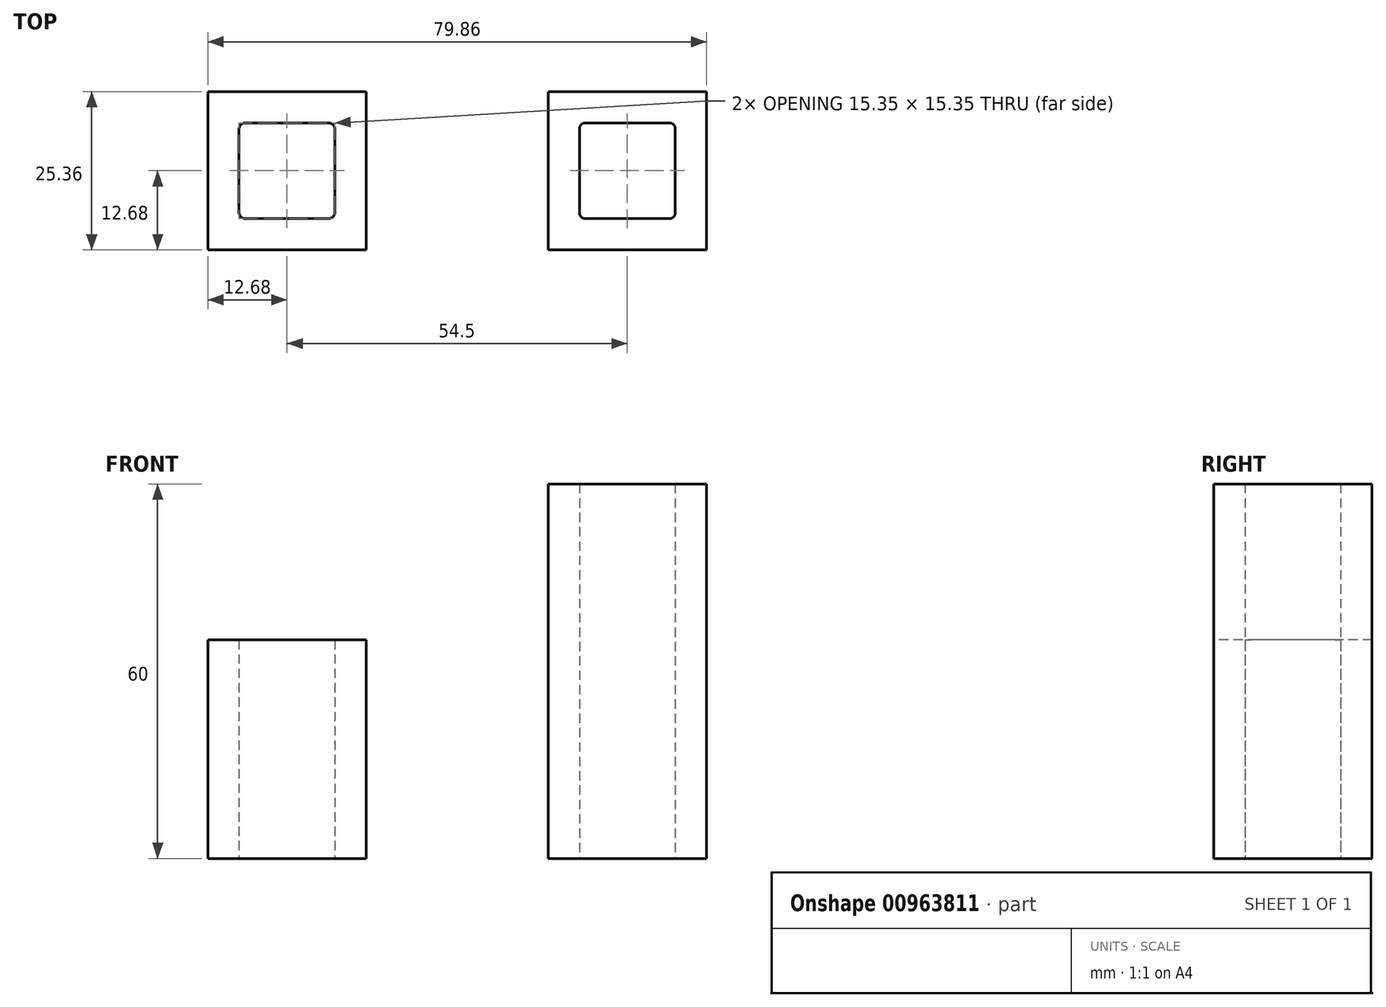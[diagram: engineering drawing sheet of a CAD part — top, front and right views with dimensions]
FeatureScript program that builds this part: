
annotation { "Feature Type Name" : "Feature", "Feature Type Description" : "" }
export const myFeature = defineFeature(function(context is Context, id is Id, definition is map)
    precondition{}
    {
        {
            var Q0;
            Q0=qCreatedBy(makeId("Top.planeOp"),FACE);
            var sketch = newSketch(context, id + "F0", { "sketchPlane" : qUnion([Q0])});
            skLineSegment(sketch, "E0.bottom", {"start": v(6.67, 7.68) * mm, "end": v(-6.67, 7.68) * mm});
            skLineSegment(sketch, "E0.top", {"start": v(6.67, -7.68) * mm, "end": v(-6.68, -7.68) * mm});
            skLineSegment(sketch, "E0.left", {"start": v(7.67, 6.68) * mm, "end": v(7.67, -6.68) * mm});
            skLineSegment(sketch, "E0.right", {"start": v(-7.68, 6.68) * mm, "end": v(-7.68, -6.68) * mm});
            skPoint(sketch, "E0.middle", {"position": v(0, 0) * mm});
            skLineSegment(sketch, "E1.0", {"start": v(12.67, 12.68) * mm, "end": v(-12.68, 12.68) * mm});
            skLineSegment(sketch, "E1.1", {"start": v(12.67, 12.68) * mm, "end": v(12.67, -12.68) * mm});
            skLineSegment(sketch, "E1.2", {"start": v(12.67, -12.67) * mm, "end": v(-12.68, -12.67) * mm});
            skLineSegment(sketch, "E1.3", {"start": v(-12.68, 12.68) * mm, "end": v(-12.68, -12.68) * mm});
            skPoint(sketch, "E2.visualSharp", {"position": v(-7.67, 7.68) * mm});
            skArc(sketch, "E2.filletArc", {"start": v(-6.67, 7.68) * mm, "mid": v(-7.38, 7.38) * mm, "end": v(-7.67, 6.68) * mm});
            skPoint(sketch, "E3.visualSharp", {"position": v(7.68, 7.68) * mm});
            skArc(sketch, "E3.filletArc", {"start": v(7.68, 6.68) * mm, "mid": v(7.38, 7.38) * mm, "end": v(6.67, 7.68) * mm});
            skPoint(sketch, "E4.visualSharp", {"position": v(7.67, -7.68) * mm});
            skArc(sketch, "E4.filletArc", {"start": v(6.67, -7.68) * mm, "mid": v(7.38, -7.38) * mm, "end": v(7.68, -6.68) * mm});
            skPoint(sketch, "E5.visualSharp", {"position": v(-7.68, -7.68) * mm});
            skArc(sketch, "E5.filletArc", {"start": v(-7.68, -6.68) * mm, "mid": v(-7.38, -7.38) * mm, "end": v(-6.68, -7.68) * mm});
            skLineSegment(sketch, "E6.bottom", {"start": v(-47.83, 7.68) * mm, "end": v(-61.18, 7.68) * mm});
            skLineSegment(sketch, "E6.top", {"start": v(-47.83, -7.68) * mm, "end": v(-61.18, -7.68) * mm});
            skLineSegment(sketch, "E6.left", {"start": v(-46.83, 6.68) * mm, "end": v(-46.83, -6.68) * mm});
            skLineSegment(sketch, "E6.right", {"start": v(-62.18, 6.68) * mm, "end": v(-62.18, -6.67) * mm});
            skPoint(sketch, "E6.middle", {"position": v(-54.5, 0) * mm});
            skLineSegment(sketch, "E7.0", {"start": v(-41.83, 12.67) * mm, "end": v(-67.18, 12.67) * mm});
            skLineSegment(sketch, "E7.1", {"start": v(-41.83, 12.67) * mm, "end": v(-41.83, -12.68) * mm});
            skLineSegment(sketch, "E7.2", {"start": v(-41.83, -12.67) * mm, "end": v(-67.18, -12.67) * mm});
            skLineSegment(sketch, "E7.3", {"start": v(-67.18, 12.67) * mm, "end": v(-67.18, -12.68) * mm});
            skPoint(sketch, "E8.visualSharp", {"position": v(-62.18, 7.68) * mm});
            skArc(sketch, "E8.filletArc", {"start": v(-61.18, 7.68) * mm, "mid": v(-61.88, 7.38) * mm, "end": v(-62.18, 6.68) * mm});
            skPoint(sketch, "E9.visualSharp", {"position": v(-46.83, 7.68) * mm});
            skArc(sketch, "E9.filletArc", {"start": v(-46.83, 6.68) * mm, "mid": v(-47.12, 7.38) * mm, "end": v(-47.83, 7.68) * mm});
            skPoint(sketch, "E10.visualSharp", {"position": v(-46.83, -7.68) * mm});
            skArc(sketch, "E10.filletArc", {"start": v(-47.83, -7.68) * mm, "mid": v(-47.12, -7.38) * mm, "end": v(-46.83, -6.68) * mm});
            skPoint(sketch, "E11.visualSharp", {"position": v(-62.18, -7.68) * mm});
            skArc(sketch, "E11.filletArc", {"start": v(-62.18, -6.68) * mm, "mid": v(-61.88, -7.38) * mm, "end": v(-61.18, -7.68) * mm});
            skSolve(sketch);
        }
        {
            var Q0;
            Q0=makeQuery(id+"F0.imprint","IMPRINT",FACE,{"disambiguationData":[TD([[makeQuery(id+"F0.imprint","IMPRINT",EDGE,{"derivedFrom":sQuery(id+"F0.wireOp",EDGE,"E0.bottom")}),-1.0]])]});
            extrude(context, id + "F1", {"entities" : qUnion([Q0]), "depth" : 60 * mm, "offsetDistance" : 25 * mm});
        }
        {
            var Q0;
            Q0=makeQuery(id+"F0.imprint","IMPRINT",FACE,{"disambiguationData":[TD([[makeQuery(id+"F0.imprint","IMPRINT",EDGE,{"derivedFrom":sQuery(id+"F0.wireOp",EDGE,"E6.bottom")}),-1.0]])]});
            extrude(context, id + "F2", {"entities" : qUnion([Q0]), "depth" : 35 * mm, "offsetDistance" : 25 * mm});
        }
    });
